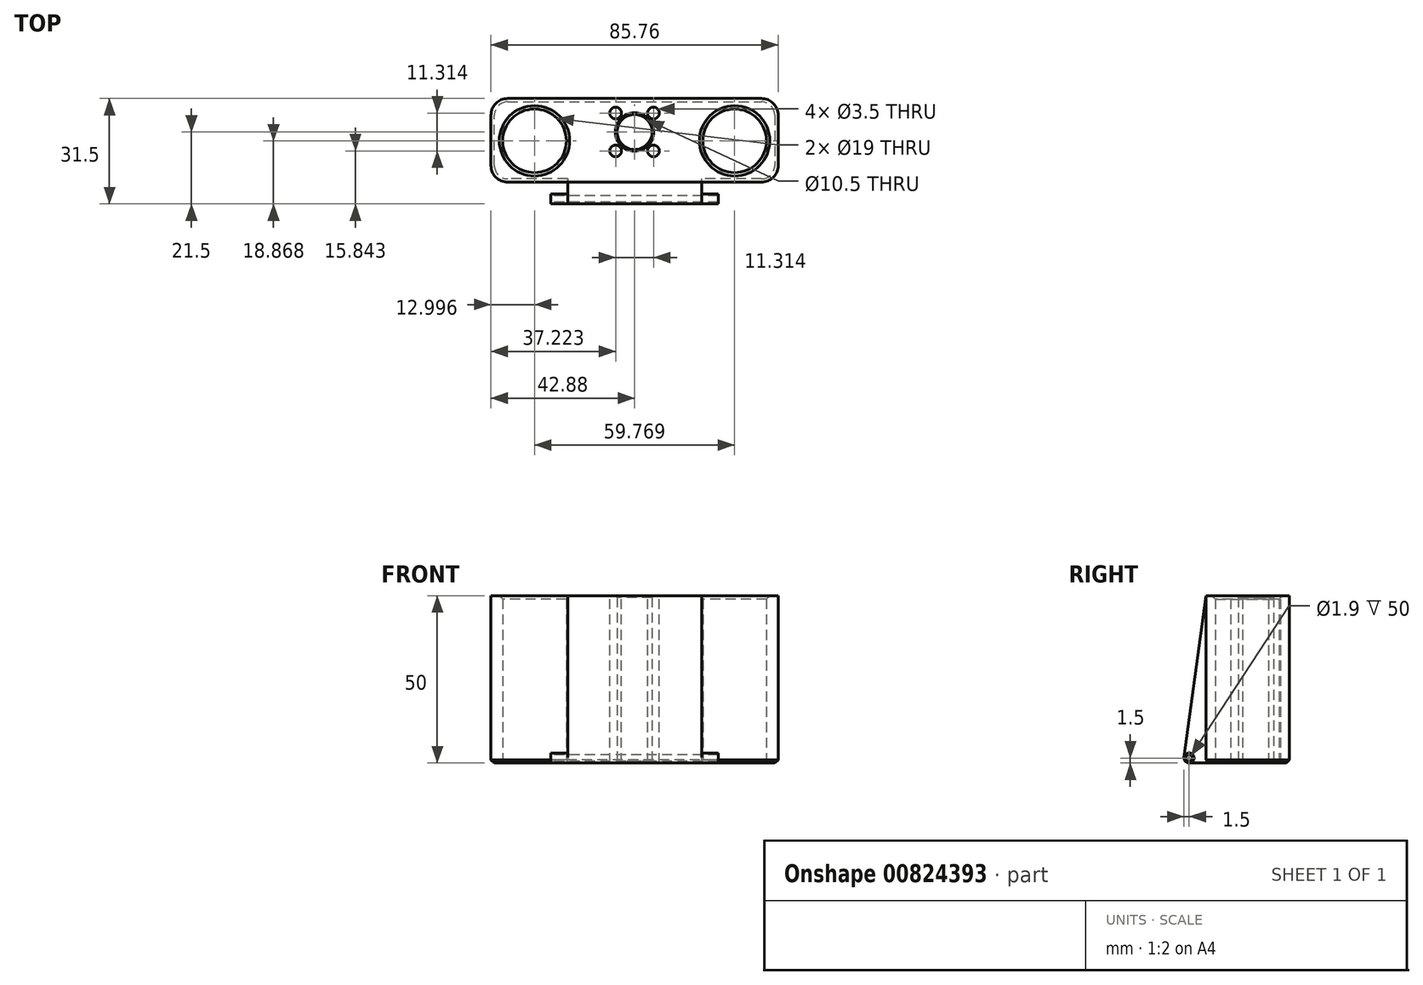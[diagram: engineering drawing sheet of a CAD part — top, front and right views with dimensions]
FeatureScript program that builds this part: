
annotation { "Feature Type Name" : "Feature", "Feature Type Description" : "" }
export const myFeature = defineFeature(function(context is Context, id is Id, definition is map)
    precondition{}
    {
        {
            var Q0;
            Q0=qCreatedBy(makeId("Top.planeOp"),FACE);
            var sketch = newSketch(context, id + "F0", { "sketchPlane" : qUnion([Q0])});
            skCircle(sketch, "E0", {"center": v(0, 0) * mm, "radius": 171 * mm, "construction": true});
            skCircle(sketch, "E1", {"center": v(0, 171) * mm, "radius": 30 * mm, "construction": true});
            skPoint(sketch, "E2", {"position": v(-29.88, 168.37) * mm});
            skPoint(sketch, "E3", {"position": v(29.88, 168.37) * mm});
            skCircle(sketch, "E4", {"center": v(-29.88, 168.37) * mm, "radius": 9.5 * mm});
            skLineSegment(sketch, "E5.bottom", {"start": v(-42.88, 181) * mm, "end": v(42.88, 181) * mm});
            skLineSegment(sketch, "E5.top", {"start": v(-42.88, 156) * mm, "end": v(42.88, 156) * mm});
            skLineSegment(sketch, "E5.left", {"start": v(-42.88, 181) * mm, "end": v(-42.88, 156) * mm});
            skLineSegment(sketch, "E5.right", {"start": v(42.88, 181) * mm, "end": v(42.88, 156) * mm});
            skPoint(sketch, "E6", {"position": v(0, 181) * mm});
            skCircle(sketch, "E7", {"center": v(29.88, 168.37) * mm, "radius": 9.5 * mm});
            skCircle(sketch, "E8", {"center": v(0, 171) * mm, "radius": 5.25 * mm});
            skSolve(sketch);
        }
        {
            var Q0;
            Q0=makeQuery(id+"F0.imprint","IMPRINT",FACE,{"disambiguationData":[TD([[makeQuery(id+"F0.imprint","IMPRINT",EDGE,{"derivedFrom":sQuery(id+"F0.wireOp",EDGE,"E4")}),-1.0]])]});
            var Q1;
            Q1=sQuery(id+"F0.wireOp",EDGE,"E1");
            var Q2;
            Q2=sQuery(id+"F0.wireOp",EDGE,"E0");
            extrude(context, id + "F1", {"entities" : qUnion([Q0]), "surfaceEntities" : qUnion([Q1, Q2]), "depth" : 50 * mm, "offsetDistance" : 25 * mm});
        }
        {
            var Q0;
            Q0=makeQuery(id+"F1.opExtrude","SWEPT_FACE",FACE,{"disambiguationData":[OSD([sQuery(id+"F0.wireOp",EDGE,"E5.right")])]});
            var Q1;
            Q1=makeQuery(id+"F1.opExtrude","SWEPT_FACE",FACE,{"disambiguationData":[OSD([sQuery(id+"F0.wireOp",EDGE,"E5.left")])]});
            cPlane(context, id + "F2", {"entities" : qUnion([Q0, Q1]), "cplaneType" : CPlaneType.MID_PLANE, "offset" : 25 * mm, "width" : 150 * mm, "height" : 150 * mm});
        }
        {
            var Q0;
            Q0=qCreatedBy(id+"F2.planeOp",FACE);
            var sketch = newSketch(context, id + "F3", { "sketchPlane" : qUnion([Q0])});
            skCircle(sketch, "E9", {"center": v(151, 1.5) * mm, "radius": 0.95 * mm});
            skArc(sketch, "E10", {"start": v(151, 3) * mm, "mid": v(149.5, 1.5) * mm, "end": v(151, 0) * mm});
            skLineSegment(sketch, "E11.0", {"start": v(156, 50) * mm, "end": v(156, 0) * mm});
            skPoint(sketch, "E12", {"position": v(156, 25) * mm});
            skCircle(sketch, "E13", {"center": v(151, 1.5) * mm, "radius": 4 * mm, "construction": true});
            skLineSegment(sketch, "E14", {"start": v(151, 3) * mm, "end": v(151, 0) * mm, "construction": true});
            skLineSegment(sketch, "E15", {"start": v(151, 0) * mm, "end": v(156, 0) * mm});
            skLineSegment(sketch, "E16", {"start": v(149.51, 1.7) * mm, "end": v(156, 50) * mm});
            skSolve(sketch);
        }
        {
            var Q0;
            Q0=makeQuery(id+"F3.imprint","IMPRINT",FACE,{"disambiguationData":[TD([[makeQuery(id+"F3.imprint","IMPRINT",EDGE,{"derivedFrom":sQuery(id+"F3.wireOp",EDGE,"E9")}),-1.0]])]});
            extrude(context, id + "F4", {"entities" : qUnion([Q0]), "operationType" : NewBodyOperationType.ADD, "endBound" : BoundingType.SYMMETRIC, "depth" : 40 * mm, "offsetDistance" : 25 * mm});
        }
        {
            var Q0;
            Q0=makeQuery(id+"F4.opExtrude","CAP_FACE",FACE,{"disambiguationData":[OSD([sQuery(id+"F3.wireOp",EDGE,"E9"),sQuery(id+"F3.wireOp",EDGE,"E10"),sQuery(id+"F3.wireOp",EDGE,"E11.0"),sQuery(id+"F3.wireOp",EDGE,"gG6s2vWR-44jh-Br3p-PvT8-iBZuAoDY5pb1"),sQuery(id+"F3.wireOp",EDGE,"E15")])],"isStart":false});
            var sketch = newSketch(context, id + "F5", { "sketchPlane" : qUnion([Q0])});
            skCircle(sketch, "E17", {"center": v(151, 1.5) * mm, "radius": 0.95 * mm});
            skCircle(sketch, "E18", {"center": v(151, 1.5) * mm, "radius": 1.5 * mm});
            skSolve(sketch);
        }
        {
            var Q0;
            Q0=makeQuery(id+"F5.imprint","IMPRINT",FACE,{"disambiguationData":[TD([[makeQuery(id+"F5.imprint","IMPRINT",EDGE,{"derivedFrom":sQuery(id+"F5.wireOp",EDGE,"E17")}),-1.0]])]});
            extrude(context, id + "F6", {"entities" : qUnion([Q0]), "operationType" : NewBodyOperationType.ADD, "depth" : 5 * mm, "offsetDistance" : 25 * mm});
        }
        {
            var Q0;
            Q0=makeQuery(id+"F4.opExtrude","CAP_FACE",FACE,{"disambiguationData":[OSD([sQuery(id+"F3.wireOp",EDGE,"E9"),sQuery(id+"F3.wireOp",EDGE,"E10"),sQuery(id+"F3.wireOp",EDGE,"E11.0"),sQuery(id+"F3.wireOp",EDGE,"gG6s2vWR-44jh-Br3p-PvT8-iBZuAoDY5pb1"),sQuery(id+"F3.wireOp",EDGE,"E15")])],"isStart":true});
            var sketch = newSketch(context, id + "F7", { "sketchPlane" : qUnion([Q0])});
            skCircle(sketch, "E19", {"center": v(-151, 1.5) * mm, "radius": 0.95 * mm});
            skCircle(sketch, "E20", {"center": v(-151, 1.5) * mm, "radius": 1.5 * mm});
            skSolve(sketch);
        }
        {
            var Q0;
            Q0=makeQuery(id+"F7.imprint","IMPRINT",FACE,{"disambiguationData":[TD([[makeQuery(id+"F7.imprint","IMPRINT",EDGE,{"derivedFrom":sQuery(id+"F7.wireOp",EDGE,"E19")}),1.0]])]});
            extrude(context, id + "F8", {"entities" : qUnion([Q0]), "operationType" : NewBodyOperationType.ADD, "depth" : 5 * mm, "offsetDistance" : 25 * mm});
        }
        {
            var Q0;
            Q0=makeQuery(id+"F1.opExtrude","CAP_FACE",FACE,{"disambiguationData":[OSD([sQuery(id+"F0.wireOp",EDGE,"E4"),sQuery(id+"F0.wireOp",EDGE,"E5.bottom"),sQuery(id+"F0.wireOp",EDGE,"E5.top"),sQuery(id+"F0.wireOp",EDGE,"E5.left"),sQuery(id+"F0.wireOp",EDGE,"E5.right"),sQuery(id+"F0.wireOp",EDGE,"E7"),sQuery(id+"F0.wireOp",EDGE,"E8")])],"isStart":false});
            var sketch = newSketch(context, id + "F9", { "sketchPlane" : qUnion([Q0])});
            skPoint(sketch, "E21", {"position": v(0, 171) * mm});
            skCircle(sketch, "E22", {"center": v(0, 171) * mm, "radius": 8 * mm, "construction": true});
            skCircle(sketch, "E23", {"center": v(-5.66, 176.66) * mm, "radius": 1.75 * mm});
            skCircle(sketch, "E24.1.0", {"center": v(-5.66, 165.34) * mm, "radius": 1.75 * mm});
            skCircle(sketch, "E24.2.0", {"center": v(5.66, 165.34) * mm, "radius": 1.75 * mm});
            skCircle(sketch, "E24.3.0", {"center": v(5.66, 176.66) * mm, "radius": 1.75 * mm});
            skLineSegment(sketch, "E25", {"start": v(0, 171) * mm, "end": v(-8, 171) * mm, "construction": true});
            skLineSegment(sketch, "E26", {"start": v(-5.66, 176.66) * mm, "end": v(0, 171) * mm, "construction": true});
            skSolve(sketch);
        }
        {
            var Q0;
            Q0=makeQuery(id+"F9.imprint","IMPRINT",FACE,{"disambiguationData":[TD([[makeQuery(id+"F9.imprint","IMPRINT",EDGE,{"derivedFrom":sQuery(id+"F9.wireOp",EDGE,"E24.3.0")}),1.0]])]});
            var Q1;
            Q1=makeQuery(id+"F9.imprint","IMPRINT",FACE,{"disambiguationData":[TD([[makeQuery(id+"F9.imprint","IMPRINT",EDGE,{"derivedFrom":sQuery(id+"F9.wireOp",EDGE,"E23")}),1.0]])]});
            var Q2;
            Q2=makeQuery(id+"F9.imprint","IMPRINT",FACE,{"disambiguationData":[TD([[makeQuery(id+"F9.imprint","IMPRINT",EDGE,{"derivedFrom":sQuery(id+"F9.wireOp",EDGE,"E24.1.0")}),1.0]])]});
            var Q3;
            Q3=makeQuery(id+"F9.imprint","IMPRINT",FACE,{"disambiguationData":[TD([[makeQuery(id+"F9.imprint","IMPRINT",EDGE,{"derivedFrom":sQuery(id+"F9.wireOp",EDGE,"E24.2.0")}),1.0]])]});
            var Q4;
            Q4=makeQuery(id+"F4.boolean.opBoolean","MERGE",FACE,{"derivedFrom":[makeQuery(id+"F1.opExtrude","CAP_FACE",FACE,{"disambiguationData":[OSD([sQuery(id+"F0.wireOp",EDGE,"E4"),sQuery(id+"F0.wireOp",EDGE,"E5.bottom"),sQuery(id+"F0.wireOp",EDGE,"E5.top"),sQuery(id+"F0.wireOp",EDGE,"E5.left"),sQuery(id+"F0.wireOp",EDGE,"E5.right"),sQuery(id+"F0.wireOp",EDGE,"E7"),sQuery(id+"F0.wireOp",EDGE,"E8")])],"isStart":true}),makeQuery(id+"F4.opExtrude","SWEPT_FACE",FACE,{"disambiguationData":[OSD([sQuery(id+"F3.wireOp",EDGE,"E15")])]})]});
            extrude(context, id + "F10", {"entities" : qUnion([Q0, Q1, Q2, Q3]), "operationType" : NewBodyOperationType.REMOVE, "endBound" : BoundingType.UP_TO_SURFACE, "oppositeDirection" : true, "depth" : 25 * mm, "endBoundEntityFace" : qUnion([Q4]), "offsetDistance" : 25 * mm});
        }
        {
            var Q0;
            Q0=makeQuery(id+"F1.opExtrude","SWEPT_EDGE",EDGE,{"disambiguationData":[OSD([sQuery(id+"F0.wireOp",EDGE,"E5.top"),sQuery(id+"F0.wireOp",EDGE,"E5.right")])]});
            var Q1;
            Q1=makeQuery(id+"F1.opExtrude","SWEPT_EDGE",EDGE,{"disambiguationData":[OSD([sQuery(id+"F0.wireOp",EDGE,"E5.bottom"),sQuery(id+"F0.wireOp",EDGE,"E5.right")])]});
            var Q2;
            Q2=makeQuery(id+"F1.opExtrude","SWEPT_EDGE",EDGE,{"disambiguationData":[OSD([sQuery(id+"F0.wireOp",EDGE,"E5.bottom"),sQuery(id+"F0.wireOp",EDGE,"E5.left")])]});
            var Q3;
            Q3=makeQuery(id+"F1.opExtrude","SWEPT_EDGE",EDGE,{"disambiguationData":[OSD([sQuery(id+"F0.wireOp",EDGE,"E5.top"),sQuery(id+"F0.wireOp",EDGE,"E5.left")])]});
            fillet(context, id + "F11", {"entities" : qUnion([Q0, Q1, Q2, Q3]), "radius" : 5 * mm, "tangentPropagation" : true, "allowEdgeOverflow" : false});
        }
        {
            var Q0;
            Q0=makeQuery(id+"F1.opExtrude","CAP_EDGE",EDGE,{"disambiguationData":[OSD([sQuery(id+"F0.wireOp",EDGE,"E7")])],"isStart":false});
            var Q1;
            Q1=makeQuery(id+"F1.opExtrude","CAP_EDGE",EDGE,{"disambiguationData":[OSD([sQuery(id+"F0.wireOp",EDGE,"E4")])],"isStart":false});
            var Q2;
            Q2=makeQuery(id+"F1.opExtrude","CAP_EDGE",EDGE,{"disambiguationData":[OSD([sQuery(id+"F0.wireOp",EDGE,"E7")])],"isStart":true});
            var Q3;
            Q3=makeQuery(id+"F1.opExtrude","CAP_EDGE",EDGE,{"disambiguationData":[OSD([sQuery(id+"F0.wireOp",EDGE,"E4")])],"isStart":true});
            chamfer(context, id + "F12", {"entities" : qUnion([Q0, Q1, Q2, Q3]), "width" : 1 * mm, "tangentPropagation" : true});
        }
        {
            var Q0;
            Q0=makeQuery(id+"F1.opExtrude","CAP_EDGE",EDGE,{"disambiguationData":[OSD([sQuery(id+"F0.wireOp",EDGE,"E8")])],"isStart":false});
            var Q1;
            Q1=makeQuery(id+"F1.opExtrude","CAP_EDGE",EDGE,{"disambiguationData":[OSD([sQuery(id+"F0.wireOp",EDGE,"E8")])],"isStart":true});
            chamfer(context, id + "F13", {"entities" : qUnion([Q0, Q1]), "width" : 0.5 * mm, "tangentPropagation" : true});
        }
        {
            var Q0;
            {var subQ1=sQuery(id+"F0.wireOp",EDGE,"E5.left");var subQ2=sQuery(id+"F0.wireOp",EDGE,"E5.top");Q0=makeQuery(id+"F4.boolean.opBoolean","SPLIT",EDGE,{"disambiguationData":[TD([makeQuery(id+"F1.opExtrude","SWEPT_FACE",FACE,{"disambiguationData":[OSD([subQ1])]})])],"derivedFrom":makeQuery(id+"F1.opExtrude","CAP_EDGE",EDGE,{"disambiguationData":[OSD([subQ2])],"isStart":true})});}
            var Q1;
            {var subQ0=sQuery(id+"F0.wireOp",EDGE,"E5.left");var subQ1=sQuery(id+"F0.wireOp",EDGE,"E5.top");Q1=makeQuery(id+"F11.opFillet","BLEND_EDGE",EDGE,{"blendedFrom":[makeQuery(id+"F1.opExtrude","SWEPT_EDGE",EDGE,{"disambiguationData":[OSD([subQ1,subQ0])]}),makeQuery(id+"F4.boolean.opBoolean","MERGE",FACE,{"derivedFrom":[makeQuery(id+"F1.opExtrude","CAP_FACE",FACE,{"disambiguationData":[OSD([sQuery(id+"F0.wireOp",EDGE,"E4"),sQuery(id+"F0.wireOp",EDGE,"E5.bottom"),subQ1,subQ0,sQuery(id+"F0.wireOp",EDGE,"E5.right"),sQuery(id+"F0.wireOp",EDGE,"E7"),sQuery(id+"F0.wireOp",EDGE,"E8")])],"isStart":true}),makeQuery(id+"F4.opExtrude","SWEPT_FACE",FACE,{"disambiguationData":[OSD([sQuery(id+"F3.wireOp",EDGE,"E15")])]})]})],"blendedInto":[makeQuery(id+"F4.boolean.opBoolean","MERGE",FACE,{"derivedFrom":[makeQuery(id+"F1.opExtrude","CAP_FACE",FACE,{"disambiguationData":[OSD([sQuery(id+"F0.wireOp",EDGE,"E4"),sQuery(id+"F0.wireOp",EDGE,"E5.bottom"),subQ1,subQ0,sQuery(id+"F0.wireOp",EDGE,"E5.right"),sQuery(id+"F0.wireOp",EDGE,"E7"),sQuery(id+"F0.wireOp",EDGE,"E8")])],"isStart":true}),makeQuery(id+"F4.opExtrude","SWEPT_FACE",FACE,{"disambiguationData":[OSD([sQuery(id+"F3.wireOp",EDGE,"E15")])]})]})]});}
            chamfer(context, id + "F14", {"entities" : qUnion([Q0, Q1]), "width" : 1 * mm, "tangentPropagation" : true});
        }
    });
